# Revit family: Sanitary_Toilet-Seats_DURAVIT-AG_D-Neo-Toilet-seat-002169
name_source: partatom
category: Specialty Equipment
revit_build: Autodesk Revit 2018 (Build: 20180329_1100(x64)
units: mm (PartAtom-declared; Revit-internal decimal feet)

## family parameters
Always vertical = No
Cut with Voids When Loaded = No
OmniClass Number = 23.31.19.19.17
OmniClass Title = Water Closet Seats
Part Type = Normal
Room Calculation Point = No
Round Connector Dimension = Use Diameter
Shared = No
Work Plane-Based = Yes

## types (1)
- D-Neo Toilet seat - 002169
    BIMobject category = Toilet Seats
    Date of publishing = 14.05.2021 00:00:00
    Default Elevation = 1219.2 mm  [stored 4 ft]
    Description = Duravit D-Neo Toilet seat White 376x441x43 mm - 0021690000
    ETIM classification = EC011196 | Toilet seat
    Edition number = 1
    IFC Classification = Sanitary Terminal
    Installation instructions = https://duravit-public-assets.s3.eu-central-1.amazonaws.com
    Main material = Duravit - Plastic - 00 - White Alpin
    Manufacturer = Duravit
    Manufacturer name = DURAVIT AG
    Masterformat 2014 Code = 22 41 13.13
    Masterformat 2014 Description = Residential Water Closets
    Material main = Duroplast
    Model = D-Neo Toilet seat - 002169
    OmniClass Code = 23-31 19 19 17
    OmniClass Description = Water Closet Seats
    Product Guid = b7d328ad-5f5f-4e97-9899-a00f82ec133f
    Product SKU = d-neo-toilet-seat-002169
    Product certification = https://pro.duravit.com
    Product data url = https://bimobject.com
    Product family = D-Neo
    Product group = Toilet seat
    Product name = D-Neo Toilet seat - 002169
    Product url = https://pro.duravit.com
    QR code = https://bimobject.com
    Technical description = https://pro.duravit.com
    UNSPSC Code = 301815
    URL = https://www.duravit.com
    Uniclass 2015 Code = Pr_40_20_93_95
    Uniclass 2015 Name = WC seats and covers
    Uniformat II Code = D2010
    Uniformat II Description = Plumbing Fixtures
    Weight Net (Kg) = 2,4
    Youtube clip = https://pro.duravit.com

note: [stored X ft] marks values corroborated as IEEE doubles in the binary element streams (Revit-internal decimal feet)

## geometry (parser evidence)
native form markers: Sweep x3
no freeform markers — native parametric forms only
